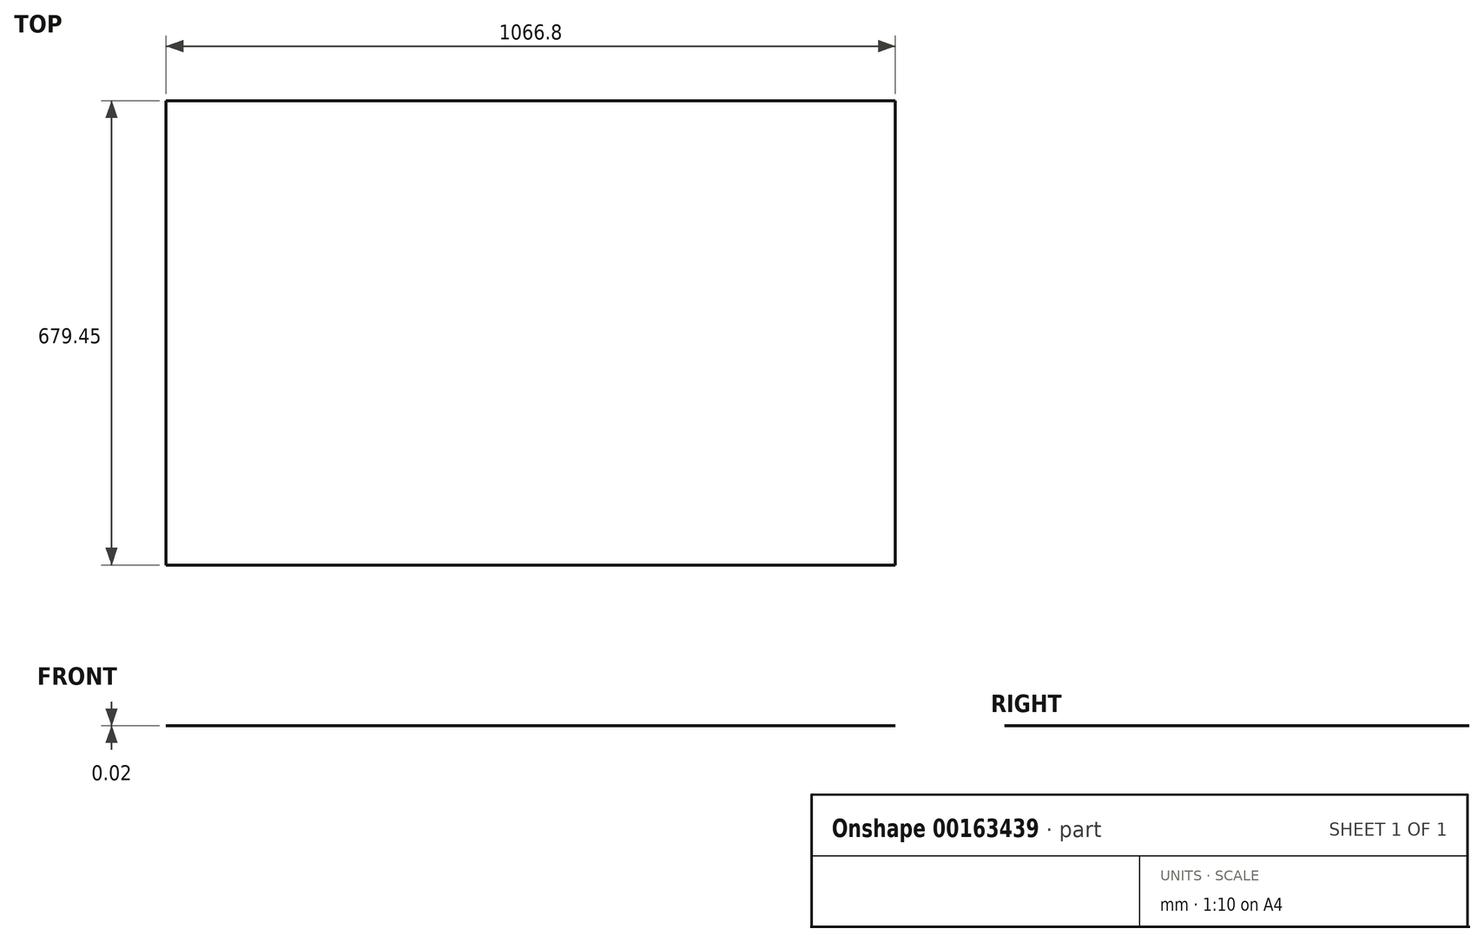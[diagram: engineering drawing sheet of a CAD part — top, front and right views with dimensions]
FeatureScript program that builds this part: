
annotation { "Feature Type Name" : "Feature", "Feature Type Description" : "" }
export const myFeature = defineFeature(function(context is Context, id is Id, definition is map)
    precondition{}
    {
        {
            var Q0;
            Q0=qCreatedBy(makeId("Top.planeOp"),FACE);
            var sketch = newSketch(context, id + "F0", { "sketchPlane" : qUnion([Q0])});
            skLineSegment(sketch, "E0.bottom", {"start": v(0, 0) * mm, "end": v(1066.8, 0) * mm});
            skLineSegment(sketch, "E0.top", {"start": v(0, 679.45) * mm, "end": v(1066.8, 679.45) * mm});
            skLineSegment(sketch, "E0.left", {"start": v(0, 0) * mm, "end": v(0, 679.45) * mm});
            skLineSegment(sketch, "E0.right", {"start": v(1066.8, 0) * mm, "end": v(1066.8, 679.45) * mm});
            skSolve(sketch);
        }
        {
            var Q0;
            Q0=qSketchRegion(id+"F0",true);
            extrude(context, id + "F1", {"entities" : qUnion([Q0]), "depth" : 5 / 203.2 * mm});
        }
    });
